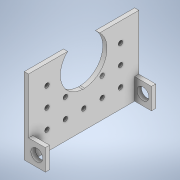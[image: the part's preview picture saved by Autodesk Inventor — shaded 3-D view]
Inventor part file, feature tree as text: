
AUTODESK INVENTOR PART (.ipt)
format: ipt  version: 2022.2 (Build 262287010, 287A)  size: 174,592 bytes
history: native  units: in
note: dims shown in document units (in); Inventor stores cm internally (conversion verified against a paired STEP export)
features: sketch x4, extrude x3, hole x1, pattern_linear x1, mirror x1
ambient origin geometry x8: Origin, YZ Plane, XZ Plane, XY Plane, X Axis, Y Axis, Z Axis, Center Point
bodies: Solid1 (feature_tree)
feature tree (10):
  extrude  "Extrusion1"  Depth=6.5in
  extrude  "Extrusion2"  Depth=2.5092in
  extrude  "Extrusion3"  Depth=0.25in
  hole  "Hole1"  [1 undecoded]
  pattern_linear  "Rectangular Pattern1"  Spacing1=0.25in  [1 undecoded]
  mirror  "Mirror2"
  sketch  "Sketch1"  dims[d0=6.5in d1=1.0in]
  sketch  "Sketch2"  dims[d2=2.75in d3=2.5092in]
  sketch  "Sketch4"  dims[d4=1.0in d5=0.25in]
  sketch  "Sketch5"  dims[d6=0.0in d7=0.25in d8=0.25in d9=0.9921in d10=0.0in d11=0.7421in d12=0.7in d13=0.0in d14=0.0in d15=1.25in d16=0.266in d17=0.75in d18=0.75in d19=0.188in d20=0.5635in d21=0.31in d22=0.0in d23=1.0833in d24=1.1273in d25=1.1811in d27=1.1273in d28=1.9685in d30=1.0833in]
note: 2 required parameter values undecoded (feature->parameter linkage not recoverable at this tier; creation-order binding heuristic only, values carry confidence <= 0.55)
